# Revit family: Rough_Valve-Central_Thermostat-American_Standard-Ceratherm-R530
name_source: partatom
category: Pipe Accessories
units: mm (PartAtom-declared; Revit-internal decimal feet)

## family parameters
Cut with Voids When Loaded = No
Host = Face
OmniClass Number = 23.65.55.14.24
OmniClass Title = Mixing Valves for Liquid Services
Part Type = Normal
Round Connector Dimension = Use Diameter
Shared = Yes

## types (2) — shared parameters
Assembly Code = D2090900
CW Connection = Yes
Cold Water Connection Diameter = 3/4"
Cold Water Connection Radius = 3/8"
Connection Distance from Finished Wall = 2"
Connection Distance from Finished Wall (2" to 2-5/8") = 2"
Default Elevation = 34"
Description = Ceratherm Central Thermostat
Finish = Metal-American Standard-Cast Brass
Finish - Lower Plastic = Plastic-American Standard-Grey
HW Connection = Yes
Height = 3 3/8"
Hot Water Connection Diameter = 3/4"
Hot Water Connection Radius = 3/8"
Installation Type = In Wall
Manufacturer = American Standard
Material = Metal-American Standard-Cast Brass
Maximum Temperature = 112°F
Model = R530
Outlet Connection Diameter = 3/4"
Price = Prices may vary. Please consult Manufacturer Representative for most up-to-date price list.
Product Documentation Link = https://www.americanstandard-us.com
Product Page URL = Cannot be found
URL = https://www.americanstandard-us.com

## per-type parameters (varying)
| type | Plaster Guard | Plaster Guard Off |
| R530 | No | Yes |
| R530 (with Plaster Guard) | Yes | No |

## geometry (parser evidence)
native form markers: Sweep x2
no freeform markers — native parametric forms only
